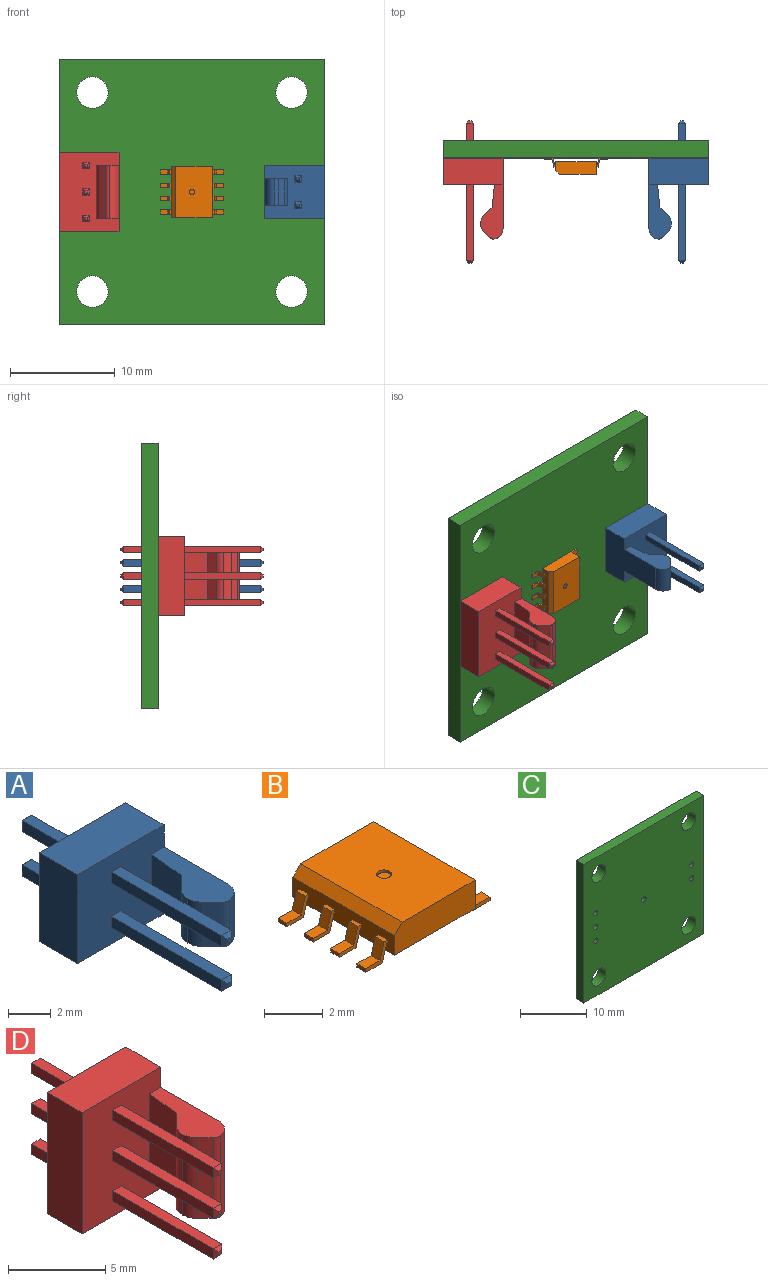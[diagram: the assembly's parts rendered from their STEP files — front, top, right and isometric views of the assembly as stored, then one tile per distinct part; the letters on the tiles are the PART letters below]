
ASSEMBLY  parts=4 mates=9
PART A: 52 faces, bbox 5.7x13.6x5.1 mm
  f0: plane 5.72x5.08mm, normal (0,-1,0), area 26.1mm2, adj f2,f3,f4,f5,f6,f7,f10,f16
  f1: plane 2.54x0.04mm, normal (-1,0,0), area 0.1mm2, adj f2,f3,f12,f13
  f2: plane 5.21x2.16mm, normal (0,0,-1), area 7.1mm2, adj f0,f1,f6,f9,f10,f11,f12,f13
  f3: plane 5.21x2.16mm, normal (0,0,1), area 7.1mm2, adj f0,f1,f6,f9,f10,f11,f12,f13
  f4: plane 5.72x2.54mm, normal (0,0,1), area 14.5mm2, adj f0,f6,f7,f8
  f5: plane 5.72x2.54mm, normal (0,0,-1), area 14.5mm2, adj f0,f6,f7,f8
  f6: plane 6.75x5.08mm, normal (1,0,0), area 23.6mm2, adj f0,f2,f3,f4,f5,f8,f15
  f7: plane 5.08x2.54mm, normal (-1,0,0), area 12.9mm2, adj f0,f4,f5,f8
  f8: plane 5.72x5.08mm, normal (0,1,0), area 28.2mm2, adj f4,f5,f6,f7,f34,f35,f36,f37
  f9: plane 2.54x0.61mm, normal (-0.71,-0.71,0), area 2.2mm2, adj f2,f3,f13,f14
  f10: plane 2.54x2.18mm, normal (-0.99,0.1,0), area 5.6mm2, adj f0,f2,f3,f11
  f11: plane 2.54x0.82mm, normal (-0.71,0.71,0), area 2.9mm2, adj f2,f3,f10,f12
  f12: cylinder r=1mm len=2.54mm, axis (0,0,-1), area 2mm2, adj f1,f2,f3,f11
  f13: cylinder r=1mm len=2.54mm, axis (0,0,-1), area 2mm2, adj f1,f2,f3,f9
  f14: cylinder r=0.5mm len=2.54mm, axis (0,0,-1), area 1mm2, adj f2,f3,f9,f15
  f15: cylinder r=1mm len=2.54mm, axis (0,0,-1), area 3.7mm2, adj f2,f3,f6,f14
  f16: plane 7.29x0.64mm, normal (0,0,1), area 4.6mm2, adj f0,f17,f19,f32
  f17: plane 7.29x0.64mm, normal (-1,0,0), area 4.6mm2, adj f0,f16,f18,f33
  f18: plane 7.29x0.64mm, normal (0,0,-1), area 4.6mm2, adj f0,f17,f19,f31
  f19: plane 7.29x0.64mm, normal (1,0,0), area 4.6mm2, adj f0,f16,f18,f30
  f20: plane 0.24x0.24mm, normal (0,-1,0), area 0.1mm2, adj f30,f31,f32,f33
  f21: plane 7.29x0.64mm, normal (-1,0,0), area 4.6mm2, adj f0,f22,f24,f29
  f22: plane 7.29x0.64mm, normal (0,0,-1), area 4.6mm2, adj f0,f21,f23,f28
  f23: plane 7.29x0.64mm, normal (1,0,0), area 4.6mm2, adj f0,f22,f24,f26
  f24: plane 7.29x0.64mm, normal (0,0,1), area 4.6mm2, adj f0,f21,f23,f27
  f25: plane 0.24x0.24mm, normal (0,-1,0), area 0.1mm2, adj f26,f27,f28,f29
  f26: plane 0.64x0.2mm, normal (0.71,-0.71,0), area 0.1mm2, adj f23,f25,f27,f28
  f27: plane 0.64x0.2mm, normal (0,-0.71,0.71), area 0.1mm2, adj f24,f25,f26,f29
  f28: plane 0.64x0.2mm, normal (0,-0.71,-0.71), area 0.1mm2, adj f22,f25,f26,f29
  f29: plane 0.64x0.2mm, normal (-0.71,-0.71,0), area 0.1mm2, adj f21,f25,f27,f28
  f30: plane 0.64x0.2mm, normal (0.71,-0.71,0), area 0.1mm2, adj f19,f20,f31,f32
  f31: plane 0.64x0.2mm, normal (0,-0.71,-0.71), area 0.1mm2, adj f18,f20,f30,f33
  f32: plane 0.64x0.2mm, normal (0,-0.71,0.71), area 0.1mm2, adj f16,f20,f30,f33
  f33: plane 0.64x0.2mm, normal (-0.71,-0.71,0), area 0.1mm2, adj f17,f20,f31,f32
  f34: plane 3.36x0.64mm, normal (0,0,-1), area 2.1mm2, adj f8,f35,f37,f48
  f35: plane 3.36x0.64mm, normal (-1,0,0), area 2.1mm2, adj f8,f34,f36,f49
  f36: plane 3.36x0.64mm, normal (0,0,1), area 2.1mm2, adj f8,f35,f37,f51
  f37: plane 3.36x0.64mm, normal (1,0,0), area 2.1mm2, adj f8,f34,f36,f50
  f38: plane 0.24x0.24mm, normal (0,1,0), area 0.1mm2, adj f48,f49,f50,f51
  f39: plane 3.36x0.64mm, normal (1,0,0), area 2.1mm2, adj f8,f40,f42,f46
  f40: plane 3.36x0.64mm, normal (0,0,-1), area 2.1mm2, adj f8,f39,f41,f44
  f41: plane 3.36x0.64mm, normal (-1,0,0), area 2.1mm2, adj f8,f40,f42,f45
  f42: plane 3.36x0.64mm, normal (0,0,1), area 2.1mm2, adj f8,f39,f41,f47
  f43: plane 0.24x0.24mm, normal (0,1,0), area 0.1mm2, adj f44,f45,f46,f47
  f44: plane 0.64x0.2mm, normal (0,0.71,-0.71), area 0.1mm2, adj f40,f43,f45,f46
  f45: plane 0.64x0.2mm, normal (-0.71,0.71,0), area 0.1mm2, adj f41,f43,f44,f47
  f46: plane 0.64x0.2mm, normal (0.71,0.71,0), area 0.1mm2, adj f39,f43,f44,f47
  f47: plane 0.64x0.2mm, normal (0,0.71,0.71), area 0.1mm2, adj f42,f43,f45,f46
  f48: plane 0.64x0.2mm, normal (0,0.71,-0.71), area 0.1mm2, adj f34,f38,f49,f50
  f49: plane 0.64x0.2mm, normal (-0.71,0.71,0), area 0.1mm2, adj f35,f38,f48,f51
  f50: plane 0.64x0.2mm, normal (0.71,0.71,0), area 0.1mm2, adj f37,f38,f48,f51
  f51: plane 0.64x0.2mm, normal (0,0.71,0.71), area 0.1mm2, adj f36,f38,f49,f50
PART B: 81 faces, bbox 6x4.9x1.6 mm
  f0: plane 0.43x0.15mm, normal (-1,0,0), area 0.1mm2, adj f4,f26,f71,f77
  f1: plane 0.43x0.15mm, normal (-1,0,0), area 0.1mm2, adj f5,f27,f75,f78
  f2: plane 0.43x0.15mm, normal (-1,0,0), area 0.1mm2, adj f6,f28,f73,f76
  f3: plane 0.43x0.15mm, normal (-1,0,0), area 0.1mm2, adj f7,f29,f72,f74
  f4: plane 0.8x0.43mm, normal (0,0,-1), area 0.3mm2, adj f0,f30,f71,f77
  f5: plane 0.8x0.43mm, normal (0,0,-1), area 0.3mm2, adj f1,f31,f75,f78
  f6: plane 0.8x0.43mm, normal (0,0,-1), area 0.3mm2, adj f2,f32,f73,f76
  f7: plane 0.8x0.43mm, normal (0,0,-1), area 0.3mm2, adj f3,f33,f72,f74
  f8: plane 0.8x0.43mm, normal (0,0,-1), area 0.3mm2, adj f12,f42,f68,f70
  f9: plane 0.8x0.43mm, normal (0,0,-1), area 0.3mm2, adj f13,f43,f66,f69
  f10: plane 0.8x0.43mm, normal (0,0,-1), area 0.3mm2, adj f14,f44,f64,f67
  f11: plane 0.8x0.43mm, normal (0,0,-1), area 0.3mm2, adj f15,f45,f63,f65
  f12: plane 0.43x0.15mm, normal (1,0,0), area 0.1mm2, adj f8,f50,f68,f70
  f13: plane 0.43x0.15mm, normal (1,0,0), area 0.1mm2, adj f9,f51,f66,f69
  f14: plane 0.43x0.15mm, normal (1,0,0), area 0.1mm2, adj f10,f52,f64,f67
  f15: plane 0.43x0.15mm, normal (1,0,0), area 0.1mm2, adj f11,f53,f63,f65
  f16: plane 3.9x1.19mm, normal (0,-1,0), area 4.6mm2, adj f58,f59,f60,f61,f62
  f17: plane 3.9x1.19mm, normal (0,1,0), area 4.6mm2, adj f58,f59,f60,f61,f62
  f18: plane 0.43x0.16mm, normal (0,0,1), area 0.1mm2, adj f22,f60,f71,f77
  f19: plane 0.43x0.16mm, normal (0,0,1), area 0.1mm2, adj f23,f60,f75,f78
  f20: plane 0.43x0.16mm, normal (0,0,1), area 0.1mm2, adj f24,f60,f73,f76
  f21: plane 0.43x0.16mm, normal (0,0,1), area 0.1mm2, adj f25,f60,f72,f74
  f22: plane 0.69x0.43mm, normal (-0.96,0,0.28), area 0.3mm2, adj f18,f26,f71,f77
  f23: plane 0.69x0.43mm, normal (-0.96,0,0.28), area 0.3mm2, adj f19,f27,f75,f78
  f24: plane 0.69x0.43mm, normal (-0.96,0,0.28), area 0.3mm2, adj f20,f28,f73,f76
  f25: plane 0.69x0.43mm, normal (-0.96,0,0.28), area 0.3mm2, adj f21,f29,f72,f74
  f26: plane 0.69x0.43mm, normal (0,0,1), area 0.3mm2, adj f0,f22,f71,f77
  f27: plane 0.69x0.43mm, normal (0,0,1), area 0.3mm2, adj f1,f23,f75,f78
  f28: plane 0.69x0.43mm, normal (0,0,1), area 0.3mm2, adj f2,f24,f73,f76
  f29: plane 0.69x0.43mm, normal (0,0,1), area 0.3mm2, adj f3,f25,f72,f74
  f30: plane 0.69x0.43mm, normal (0.96,0,-0.28), area 0.3mm2, adj f4,f34,f71,f77
  f31: plane 0.69x0.43mm, normal (0.96,0,-0.28), area 0.3mm2, adj f5,f35,f75,f78
  f32: plane 0.69x0.43mm, normal (0.96,0,-0.28), area 0.3mm2, adj f6,f36,f73,f76
  f33: plane 0.69x0.43mm, normal (0.96,0,-0.28), area 0.3mm2, adj f7,f37,f72,f74
  f34: plane 0.43x0.05mm, normal (0,0,-1), area 0mm2, adj f30,f60,f71,f77
  f35: plane 0.43x0.05mm, normal (0,0,-1), area 0mm2, adj f31,f60,f75,f78
  f36: plane 0.43x0.05mm, normal (0,0,-1), area 0mm2, adj f32,f60,f73,f76
  f37: plane 0.43x0.05mm, normal (0,0,-1), area 0mm2, adj f33,f60,f72,f74
  f38: plane 0.43x0.05mm, normal (0,0,-1), area 0mm2, adj f42,f62,f68,f70
  f39: plane 0.43x0.05mm, normal (0,0,-1), area 0mm2, adj f43,f62,f66,f69
  f40: plane 0.43x0.05mm, normal (0,0,-1), area 0mm2, adj f44,f62,f64,f67
  f41: plane 0.43x0.05mm, normal (0,0,-1), area 0mm2, adj f45,f62,f63,f65
  f42: plane 0.69x0.43mm, normal (-0.96,0,-0.28), area 0.3mm2, adj f8,f38,f68,f70
  f43: plane 0.69x0.43mm, normal (-0.96,0,-0.28), area 0.3mm2, adj f9,f39,f66,f69
  f44: plane 0.69x0.43mm, normal (-0.96,0,-0.28), area 0.3mm2, adj f10,f40,f64,f67
  f45: plane 0.69x0.43mm, normal (-0.96,0,-0.28), area 0.3mm2, adj f11,f41,f63,f65
  f46: plane 0.43x0.16mm, normal (0,0,1), area 0.1mm2, adj f54,f62,f68,f70
  f47: plane 0.43x0.16mm, normal (0,0,1), area 0.1mm2, adj f55,f62,f66,f69
  f48: plane 0.43x0.16mm, normal (0,0,1), area 0.1mm2, adj f56,f62,f64,f67
  f49: plane 0.43x0.16mm, normal (0,0,1), area 0.1mm2, adj f57,f62,f63,f65
  f50: plane 0.69x0.43mm, normal (0,0,1), area 0.3mm2, adj f12,f54,f68,f70
  f51: plane 0.69x0.43mm, normal (0,0,1), area 0.3mm2, adj f13,f55,f66,f69
  f52: plane 0.69x0.43mm, normal (0,0,1), area 0.3mm2, adj f14,f56,f64,f67
  f53: plane 0.69x0.43mm, normal (0,0,1), area 0.3mm2, adj f15,f57,f63,f65
  f54: plane 0.69x0.43mm, normal (0.96,0,0.28), area 0.3mm2, adj f46,f50,f68,f70
  f55: plane 0.69x0.43mm, normal (0.96,0,0.28), area 0.3mm2, adj f47,f51,f66,f69
  f56: plane 0.69x0.43mm, normal (0.96,0,0.28), area 0.3mm2, adj f48,f52,f64,f67
  f57: plane 0.69x0.43mm, normal (0.96,0,0.28), area 0.3mm2, adj f49,f53,f63,f65
  f58: plane 4.9x3.53mm, normal (0,0,1), area 17.1mm2, adj f16,f17,f59,f62,f79
  f59: plane 4.9x0.38mm, normal (-0.71,0,0.71), area 2.6mm2, adj f16,f17,f58,f60
  f60: plane 4.9x0.82mm, normal (-1,0,0), area 3.7mm2, adj f16,f17,f18,f19,f20,f21,f34,f35
  f61: plane 4.9x3.9mm, normal (0,0,-1), area 19.1mm2, adj f16,f17,f60,f62
  f62: plane 4.9x1.19mm, normal (1,0,0), area 5.6mm2, adj f16,f17,f38,f39,f40,f41,f46,f47
  f63: plane 1.05x0.84mm, normal (0,1,0), area 0.2mm2, adj f11,f15,f41,f45,f49,f53,f57,f62
  f64: plane 1.05x0.84mm, normal (0,1,0), area 0.2mm2, adj f10,f14,f40,f44,f48,f52,f56,f62
  f65: plane 1.05x0.84mm, normal (0,-1,0), area 0.2mm2, adj f11,f15,f41,f45,f49,f53,f57,f62
  f66: plane 1.05x0.84mm, normal (0,1,0), area 0.2mm2, adj f9,f13,f39,f43,f47,f51,f55,f62
  f67: plane 1.05x0.84mm, normal (0,-1,0), area 0.2mm2, adj f10,f14,f40,f44,f48,f52,f56,f62
  f68: plane 1.05x0.84mm, normal (0,1,0), area 0.2mm2, adj f8,f12,f38,f42,f46,f50,f54,f62
  f69: plane 1.05x0.84mm, normal (0,-1,0), area 0.2mm2, adj f9,f13,f39,f43,f47,f51,f55,f62
  f70: plane 1.05x0.84mm, normal (0,-1,0), area 0.2mm2, adj f8,f12,f38,f42,f46,f50,f54,f62
  f71: plane 1.05x0.84mm, normal (0,-1,0), area 0.2mm2, adj f0,f4,f18,f22,f26,f30,f34,f60
  f72: plane 1.05x0.84mm, normal (0,1,0), area 0.2mm2, adj f3,f7,f21,f25,f29,f33,f37,f60
  f73: plane 1.05x0.84mm, normal (0,1,0), area 0.2mm2, adj f2,f6,f20,f24,f28,f32,f36,f60
  f74: plane 1.05x0.84mm, normal (0,-1,0), area 0.2mm2, adj f3,f7,f21,f25,f29,f33,f37,f60
  f75: plane 1.05x0.84mm, normal (0,1,0), area 0.2mm2, adj f1,f5,f19,f23,f27,f31,f35,f60
  f76: plane 1.05x0.84mm, normal (0,-1,0), area 0.2mm2, adj f2,f6,f20,f24,f28,f32,f36,f60
  f77: plane 1.05x0.84mm, normal (0,1,0), area 0.2mm2, adj f0,f4,f18,f22,f26,f30,f34,f60
  f78: plane 1.05x0.84mm, normal (0,-1,0), area 0.2mm2, adj f1,f5,f19,f23,f27,f31,f35,f60
  f79: cylinder r=0.25mm len=0.5mm, axis (0,0,1), area 0.2mm2, adj f58,f80
  f80: plane 0.5x0.5mm, normal (0,0,1), area 0.2mm2, adj f79
PART C: 16 faces, bbox 25.4x1.6x25.4 mm
  f0: plane 25.4x1.62mm, normal (-1,0,0), area 41.1mm2, adj f1,f6,f8,f9
  f1: plane 25.4x1.62mm, normal (0,0,-1), area 41.1mm2, adj f0,f2,f8,f9
  f2: plane 25.4x1.62mm, normal (1,0,0), area 41.1mm2, adj f1,f6,f8,f9
  f3: cylinder r=1.5mm len=3mm, axis (0,1,0), area 15.3mm2, adj f8,f9
  f4: cylinder r=1.5mm len=3mm, axis (0,1,0), area 15.3mm2, adj f8,f9
  f5: cylinder r=1.5mm len=3mm, axis (0,1,0), area 15.3mm2, adj f8,f9
  f6: plane 25.4x1.62mm, normal (0,0,1), area 41.1mm2, adj f0,f2,f8,f9
  f7: cylinder r=1.5mm len=3mm, axis (0,1,0), area 15.3mm2, adj f8,f9
  f8: plane 25.4x25.4mm, normal (0,-1,0), area 612.9mm2, adj f0,f1,f2,f3,f4,f5,f6,f7
  f9: plane 25.4x25.4mm, normal (0,1,0), area 612.9mm2, adj f0,f1,f2,f3,f4,f5,f6,f7
  f10: cylinder r=0.5mm len=1.62mm, axis (0,-1,0), area 5.1mm2, adj f8,f9
  f11: cylinder r=0.45mm len=1.62mm, axis (0,1,0), area 4.6mm2, adj f8,f9
  f12: cylinder r=0.45mm len=1.62mm, axis (0,1,0), area 4.6mm2, adj f8,f9
  f13: cylinder r=0.45mm len=1.62mm, axis (0,1,0), area 4.6mm2, adj f8,f9
  f14: cylinder r=0.45mm len=1.62mm, axis (0,1,0), area 4.6mm2, adj f8,f9
  f15: cylinder r=0.45mm len=1.62mm, axis (0,1,0), area 4.6mm2, adj f8,f9
PART D: 70 faces, bbox 5.7x13.6x7.6 mm
  f0: plane 7.62x5.72mm, normal (0,-1,0), area 38.2mm2, adj f2,f3,f4,f5,f6,f7,f10,f16
  f1: plane 5.08x0.04mm, normal (-1,0,0), area 0.2mm2, adj f2,f3,f12,f13
  f2: plane 5.21x2.16mm, normal (0,0,-1), area 7.1mm2, adj f0,f1,f6,f9,f10,f11,f12,f13
  f3: plane 5.21x2.16mm, normal (0,0,1), area 7.1mm2, adj f0,f1,f6,f9,f10,f11,f12,f13
  f4: plane 5.72x2.54mm, normal (0,0,1), area 14.5mm2, adj f0,f6,f7,f8
  f5: plane 5.72x2.54mm, normal (0,0,-1), area 14.5mm2, adj f0,f6,f7,f8
  f6: plane 7.62x6.75mm, normal (1,0,0), area 40.8mm2, adj f0,f2,f3,f4,f5,f8,f15
  f7: plane 7.62x2.54mm, normal (-1,0,0), area 19.4mm2, adj f0,f4,f5,f8
  f8: plane 7.62x5.72mm, normal (0,1,0), area 42.3mm2, adj f4,f5,f6,f7,f43,f44,f45,f46
  f9: plane 5.08x0.61mm, normal (-0.71,-0.71,0), area 4.4mm2, adj f2,f3,f13,f14
  f10: plane 5.08x2.18mm, normal (-0.99,0.1,0), area 11.1mm2, adj f0,f2,f3,f11
  f11: plane 5.08x0.82mm, normal (-0.71,0.71,0), area 5.9mm2, adj f2,f3,f10,f12
  f12: cylinder r=1mm len=5.08mm, axis (0,0,-1), area 4mm2, adj f1,f2,f3,f11
  f13: cylinder r=1mm len=5.08mm, axis (0,0,-1), area 4mm2, adj f1,f2,f3,f9
  f14: cylinder r=0.5mm len=5.08mm, axis (0,0,-1), area 2mm2, adj f2,f3,f9,f15
  f15: cylinder r=1mm len=5.08mm, axis (0,0,-1), area 7.5mm2, adj f2,f3,f6,f14
  f16: plane 7.29x0.64mm, normal (0,0,1), area 4.6mm2, adj f0,f17,f19,f41
  f17: plane 7.29x0.64mm, normal (-1,0,0), area 4.6mm2, adj f0,f16,f18,f42
  f18: plane 7.29x0.64mm, normal (0,0,-1), area 4.6mm2, adj f0,f17,f19,f40
  f19: plane 7.29x0.64mm, normal (1,0,0), area 4.6mm2, adj f0,f16,f18,f39
  f20: plane 0.24x0.24mm, normal (0,-1,0), area 0.1mm2, adj f39,f40,f41,f42
  f21: plane 7.29x0.64mm, normal (-1,0,0), area 4.6mm2, adj f0,f22,f24,f38
  f22: plane 7.29x0.64mm, normal (0,0,-1), area 4.6mm2, adj f0,f21,f23,f37
  f23: plane 7.29x0.64mm, normal (1,0,0), area 4.6mm2, adj f0,f22,f24,f35
  f24: plane 7.29x0.64mm, normal (0,0,1), area 4.6mm2, adj f0,f21,f23,f36
  f25: plane 0.24x0.24mm, normal (0,-1,0), area 0.1mm2, adj f35,f36,f37,f38
  f26: plane 7.29x0.64mm, normal (0,0,1), area 4.6mm2, adj f0,f27,f29,f34
  f27: plane 7.29x0.64mm, normal (-1,0,0), area 4.6mm2, adj f0,f26,f28,f32
  f28: plane 7.29x0.64mm, normal (0,0,-1), area 4.6mm2, adj f0,f27,f29,f31
  f29: plane 7.29x0.64mm, normal (1,0,0), area 4.6mm2, adj f0,f26,f28,f33
  f30: plane 0.24x0.24mm, normal (0,-1,0), area 0.1mm2, adj f31,f32,f33,f34
  f31: plane 0.64x0.2mm, normal (0,-0.71,-0.71), area 0.1mm2, adj f28,f30,f32,f33
  f32: plane 0.64x0.2mm, normal (-0.71,-0.71,0), area 0.1mm2, adj f27,f30,f31,f34
  f33: plane 0.64x0.2mm, normal (0.71,-0.71,0), area 0.1mm2, adj f29,f30,f31,f34
  f34: plane 0.64x0.2mm, normal (0,-0.71,0.71), area 0.1mm2, adj f26,f30,f32,f33
  f35: plane 0.64x0.2mm, normal (0.71,-0.71,0), area 0.1mm2, adj f23,f25,f36,f37
  f36: plane 0.64x0.2mm, normal (0,-0.71,0.71), area 0.1mm2, adj f24,f25,f35,f38
  f37: plane 0.64x0.2mm, normal (0,-0.71,-0.71), area 0.1mm2, adj f22,f25,f35,f38
  f38: plane 0.64x0.2mm, normal (-0.71,-0.71,0), area 0.1mm2, adj f21,f25,f36,f37
  f39: plane 0.64x0.2mm, normal (0.71,-0.71,0), area 0.1mm2, adj f19,f20,f40,f41
  f40: plane 0.64x0.2mm, normal (0,-0.71,-0.71), area 0.1mm2, adj f18,f20,f39,f42
  f41: plane 0.64x0.2mm, normal (0,-0.71,0.71), area 0.1mm2, adj f16,f20,f39,f42
  f42: plane 0.64x0.2mm, normal (-0.71,-0.71,0), area 0.1mm2, adj f17,f20,f40,f41
  f43: plane 3.36x0.64mm, normal (0,0,-1), area 2.1mm2, adj f8,f44,f46,f66
  f44: plane 3.36x0.64mm, normal (-1,0,0), area 2.1mm2, adj f8,f43,f45,f67
  f45: plane 3.36x0.64mm, normal (0,0,1), area 2.1mm2, adj f8,f44,f46,f69
  f46: plane 3.36x0.64mm, normal (1,0,0), area 2.1mm2, adj f8,f43,f45,f68
  f47: plane 0.24x0.24mm, normal (0,1,0), area 0.1mm2, adj f66,f67,f68,f69
  f48: plane 3.36x0.64mm, normal (1,0,0), area 2.1mm2, adj f8,f49,f51,f64
  f49: plane 3.36x0.64mm, normal (0,0,-1), area 2.1mm2, adj f8,f48,f50,f62
  f50: plane 3.36x0.64mm, normal (-1,0,0), area 2.1mm2, adj f8,f49,f51,f63
  f51: plane 3.36x0.64mm, normal (0,0,1), area 2.1mm2, adj f8,f48,f50,f65
  f52: plane 0.24x0.24mm, normal (0,1,0), area 0.1mm2, adj f62,f63,f64,f65
  f53: plane 3.36x0.64mm, normal (1,0,0), area 2.1mm2, adj f8,f54,f56,f61
  f54: plane 3.36x0.64mm, normal (0,0,-1), area 2.1mm2, adj f8,f53,f55,f59
  f55: plane 3.36x0.64mm, normal (-1,0,0), area 2.1mm2, adj f8,f54,f56,f58
  f56: plane 3.36x0.64mm, normal (0,0,1), area 2.1mm2, adj f8,f53,f55,f60
  f57: plane 0.24x0.24mm, normal (0,1,0), area 0.1mm2, adj f58,f59,f60,f61
  f58: plane 0.64x0.2mm, normal (-0.71,0.71,0), area 0.1mm2, adj f55,f57,f59,f60
  f59: plane 0.64x0.2mm, normal (0,0.71,-0.71), area 0.1mm2, adj f54,f57,f58,f61
  f60: plane 0.64x0.2mm, normal (0,0.71,0.71), area 0.1mm2, adj f56,f57,f58,f61
  f61: plane 0.64x0.2mm, normal (0.71,0.71,0), area 0.1mm2, adj f53,f57,f59,f60
  f62: plane 0.64x0.2mm, normal (0,0.71,-0.71), area 0.1mm2, adj f49,f52,f63,f64
  f63: plane 0.64x0.2mm, normal (-0.71,0.71,0), area 0.1mm2, adj f50,f52,f62,f65
  f64: plane 0.64x0.2mm, normal (0.71,0.71,0), area 0.1mm2, adj f48,f52,f62,f65
  f65: plane 0.64x0.2mm, normal (0,0.71,0.71), area 0.1mm2, adj f51,f52,f63,f64
  f66: plane 0.64x0.2mm, normal (0,0.71,-0.71), area 0.1mm2, adj f43,f47,f67,f68
  f67: plane 0.64x0.2mm, normal (-0.71,0.71,0), area 0.1mm2, adj f44,f47,f66,f69
  f68: plane 0.64x0.2mm, normal (0.71,0.71,0), area 0.1mm2, adj f46,f47,f66,f69
  f69: plane 0.64x0.2mm, normal (0,0.71,0.71), area 0.1mm2, adj f45,f47,f67,f68
PLACE A rot(axis=(0,-1,0),180deg) t=(8.1,10.3,6.98)mm
PLACE B rot(axis=(1,0,0),90deg) t=(-6.55,9.94,6.89)mm
PLACE C t=(-4.6,11.92,4.44)mm
PLACE D t=(-17.3,10.3,0.63)mm
MATE cylindrical D.f52 <-> C.f11  axis (0,1,0) through (-14.76,13.86,4.44)mm
MATE cylindrical B.f79 <-> C.f10  axis (0,-1,0) through (-4.6,8.75,4.44)mm
MATE cylindrical A.f43 <-> C.f14  axis (0,1,0) through (5.56,13.86,5.71)mm
MATE planar D.f8 <-> C.f8  axis (0,1,0) through (-14.44,10.3,4.44)mm
MATE planar D.f7 <-> C.f0  axis (-1,0,0) through (-17.3,9.03,4.44)mm
MATE planar B.f6 <-> C.f10  axis (0,1,0) through (-7.2,10.3,5.07)mm
MATE planar A.f8 <-> C.f8  axis (0,1,0) through (5.23,10.3,4.44)mm
MATE planar A.f7 <-> C.f2  axis (1,0,0) through (8.1,9.03,4.44)mm
MATE parallel B.f16 <-> C.f1  axis (0,0,-1) through (-4.58,9.36,1.99)mm
